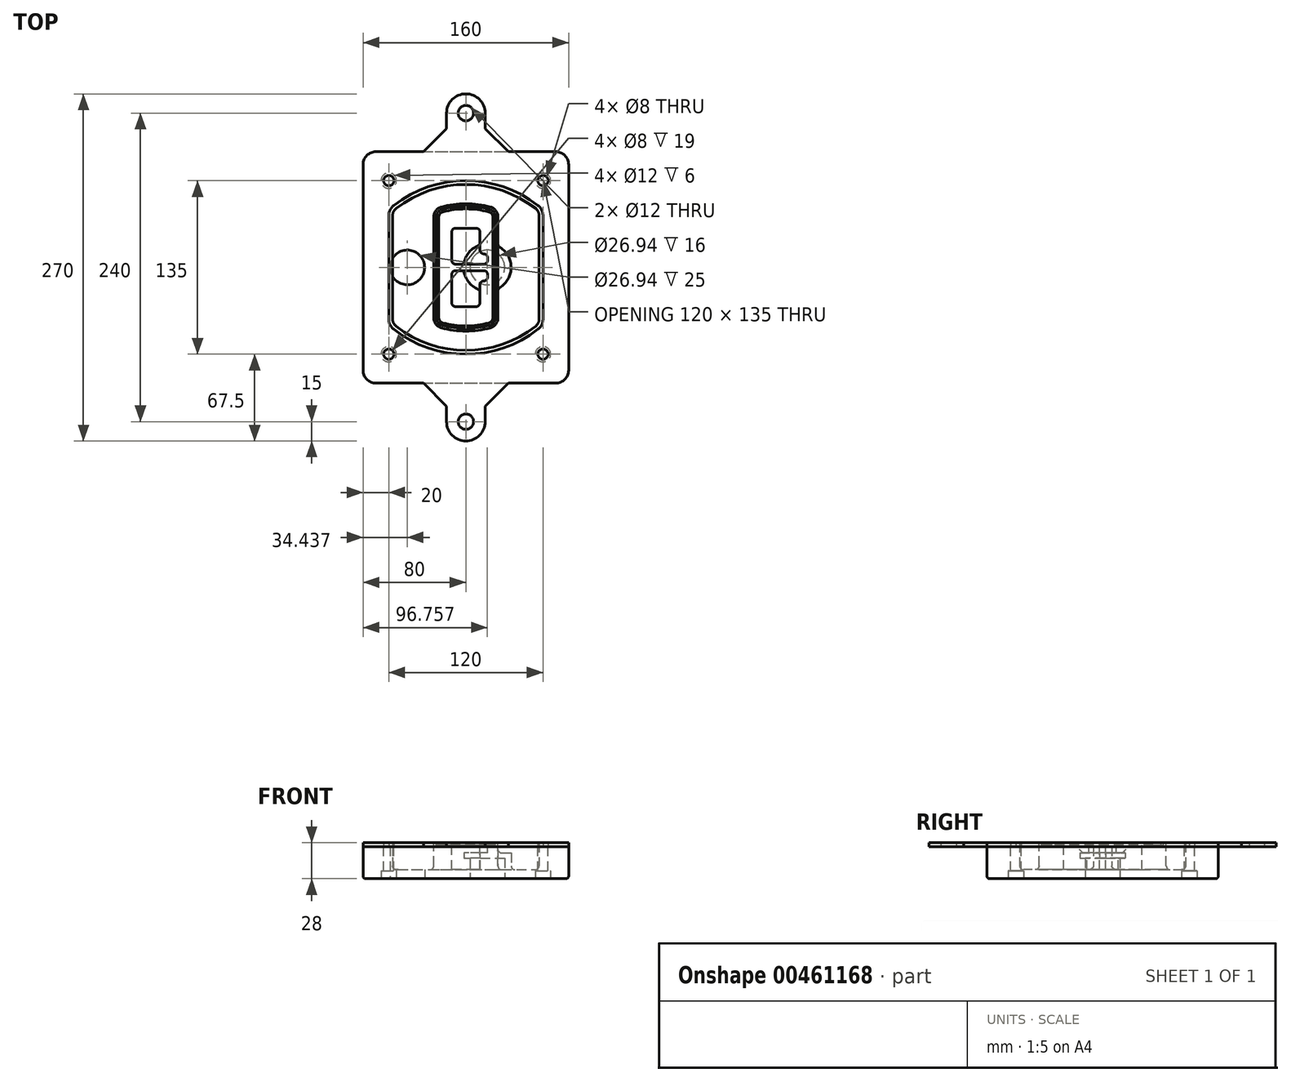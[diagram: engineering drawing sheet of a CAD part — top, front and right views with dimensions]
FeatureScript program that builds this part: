
annotation { "Feature Type Name" : "Feature", "Feature Type Description" : "" }
export const myFeature = defineFeature(function(context is Context, id is Id, definition is map)
    precondition{}
    {
        {
            var Q0;
            Q0=qCreatedBy(makeId("Top.planeOp"),FACE);
            var sketch = newSketch(context, id + "F0", { "sketchPlane" : qUnion([Q0])});
            skPoint(sketch, "E0.rect.middle", {"position": v(0, 0) * mm});
            skLineSegment(sketch, "E1.bottom", {"start": v(-70, -90) * mm, "end": v(70, -90) * mm});
            skLineSegment(sketch, "E1.top", {"start": v(-70, 90) * mm, "end": v(70, 90) * mm});
            skLineSegment(sketch, "E1.left", {"start": v(-80, -80) * mm, "end": v(-80, 80) * mm});
            skLineSegment(sketch, "E1.right", {"start": v(80, -80) * mm, "end": v(80, 80) * mm});
            skLineSegment(sketch, "E2", {"start": v(-80, 90) * mm, "end": v(80, -90) * mm, "construction": true});
            skLineSegment(sketch, "E3", {"start": v(80, 90) * mm, "end": v(-80, -90) * mm, "construction": true});
            skCircle(sketch, "E4", {"center": v(-60, 67.5) * mm, "radius": 4 * mm});
            skCircle(sketch, "E5", {"center": v(60, 67.5) * mm, "radius": 4 * mm});
            skCircle(sketch, "E6", {"center": v(60, -67.5) * mm, "radius": 4 * mm});
            skCircle(sketch, "E7", {"center": v(-60, -67.5) * mm, "radius": 4 * mm});
            skLineSegment(sketch, "E8", {"start": v(-60, 67.5) * mm, "end": v(60, 67.5) * mm, "construction": true});
            skLineSegment(sketch, "E9", {"start": v(60, 67.5) * mm, "end": v(60, -67.5) * mm, "construction": true});
            skLineSegment(sketch, "E10", {"start": v(60, -67.5) * mm, "end": v(-60, -67.5) * mm, "construction": true});
            skLineSegment(sketch, "E11", {"start": v(-60, -67.5) * mm, "end": v(-60, 67.5) * mm, "construction": true});
            skLineSegment(sketch, "E12", {"start": v(-60, 40.3) * mm, "end": v(-60, -40.3) * mm});
            skLineSegment(sketch, "E13", {"start": v(60, 40.3) * mm, "end": v(60, -40.3) * mm});
            skArc(sketch, "E14", {"start": v(56.15, 48.18) * mm, "mid": v(0, 67.5) * mm, "end": v(-56.15, 48.18) * mm});
            skArc(sketch, "E15", {"start": v(-56.15, -48.18) * mm, "mid": v(0, -67.5) * mm, "end": v(56.15, -48.18) * mm});
            skLineSegment(sketch, "E16", {"start": v(-60, 0) * mm, "end": v(60, 0) * mm, "construction": true});
            skPoint(sketch, "E17.visualSharp", {"position": v(-60, -45) * mm});
            skArc(sketch, "E17.filletArc", {"start": v(-60, -40.3) * mm, "mid": v(-58.99, -44.68) * mm, "end": v(-56.15, -48.18) * mm});
            skPoint(sketch, "E18.visualSharp", {"position": v(-60, 45) * mm});
            skArc(sketch, "E18.filletArc", {"start": v(-56.15, 48.18) * mm, "mid": v(-58.99, 44.68) * mm, "end": v(-60, 40.3) * mm});
            skPoint(sketch, "E19.visualSharp", {"position": v(60, 45) * mm});
            skArc(sketch, "E19.filletArc", {"start": v(60, 40.3) * mm, "mid": v(58.99, 44.68) * mm, "end": v(56.15, 48.18) * mm});
            skPoint(sketch, "E20.visualSharp", {"position": v(60, -45) * mm});
            skArc(sketch, "E20.filletArc", {"start": v(56.15, -48.18) * mm, "mid": v(58.99, -44.68) * mm, "end": v(60, -40.3) * mm});
            skPoint(sketch, "E21.visualSharp", {"position": v(-80, 90) * mm});
            skArc(sketch, "E21.filletArc", {"start": v(-70, 90) * mm, "mid": v(-77.07, 87.07) * mm, "end": v(-80, 80) * mm});
            skPoint(sketch, "E22.visualSharp", {"position": v(80, 90) * mm});
            skArc(sketch, "E22.filletArc", {"start": v(80, 80) * mm, "mid": v(77.07, 87.07) * mm, "end": v(70, 90) * mm});
            skPoint(sketch, "E23.visualSharp", {"position": v(80, -90) * mm});
            skArc(sketch, "E23.filletArc", {"start": v(70, -90) * mm, "mid": v(77.07, -87.07) * mm, "end": v(80, -80) * mm});
            skPoint(sketch, "E24.visualSharp", {"position": v(-80, -90) * mm});
            skArc(sketch, "E24.filletArc", {"start": v(-80, -80) * mm, "mid": v(-77.07, -87.07) * mm, "end": v(-70, -90) * mm});
            skArc(sketch, "E25.0", {"start": v(57, 40.3) * mm, "mid": v(56.3, 43.36) * mm, "end": v(54.3, 45.81) * mm});
            skLineSegment(sketch, "E25.1", {"start": v(57, 40.3) * mm, "end": v(57, -40.3) * mm});
            skArc(sketch, "E25.2", {"start": v(54.3, -45.81) * mm, "mid": v(56.3, -43.36) * mm, "end": v(57, -40.3) * mm});
            skArc(sketch, "E25.3", {"start": v(-54.3, -45.81) * mm, "mid": v(0, -64.5) * mm, "end": v(54.3, -45.81) * mm});
            skArc(sketch, "E25.4", {"start": v(-57, -40.3) * mm, "mid": v(-56.3, -43.36) * mm, "end": v(-54.3, -45.81) * mm});
            skArc(sketch, "E25.5", {"start": v(54.3, 45.81) * mm, "mid": v(0, 64.5) * mm, "end": v(-54.3, 45.81) * mm});
            skLineSegment(sketch, "E25.6", {"start": v(-57, 40.3) * mm, "end": v(-57, -40.3) * mm});
            skArc(sketch, "E25.7", {"start": v(-54.3, 45.81) * mm, "mid": v(-56.3, 43.36) * mm, "end": v(-57, 40.3) * mm});
            skArc(sketch, "E26.0", {"start": v(-58.62, 51.33) * mm, "mid": v(-62.58, 46.43) * mm, "end": v(-64, 40.3) * mm});
            skArc(sketch, "E26.1", {"start": v(58.62, 51.33) * mm, "mid": v(0, 71.5) * mm, "end": v(-58.62, 51.33) * mm});
            skArc(sketch, "E26.2", {"start": v(64, 40.3) * mm, "mid": v(62.58, 46.43) * mm, "end": v(58.62, 51.33) * mm});
            skLineSegment(sketch, "E26.3", {"start": v(64, 40.3) * mm, "end": v(64, -40.3) * mm});
            skArc(sketch, "E26.4", {"start": v(58.62, -51.33) * mm, "mid": v(62.58, -46.43) * mm, "end": v(64, -40.3) * mm});
            skLineSegment(sketch, "E26.5", {"start": v(-64, 40.3) * mm, "end": v(-64, -40.3) * mm});
            skArc(sketch, "E26.6", {"start": v(-58.62, -51.33) * mm, "mid": v(0, -71.5) * mm, "end": v(58.62, -51.33) * mm});
            skArc(sketch, "E26.7", {"start": v(-64, -40.3) * mm, "mid": v(-62.58, -46.43) * mm, "end": v(-58.62, -51.33) * mm});
            skSolve(sketch);
        }
        {
            var Q0;
            Q0=makeQuery(id+"F0.imprint","IMPRINT",FACE,{"disambiguationData":[TD([[makeQuery(id+"F0.imprint","IMPRINT",EDGE,{"derivedFrom":sQuery(id+"F0.wireOp",EDGE,"E1.bottom")}),1.0]])]});
            var Q1;
            Q1=makeQuery(id+"F0.imprint","IMPRINT",FACE,{"disambiguationData":[TD([[makeQuery(id+"F0.imprint","IMPRINT",EDGE,{"derivedFrom":sQuery(id+"F0.wireOp",EDGE,"E12")}),1.0]])]});
            var Q2;
            Q2=makeQuery(id+"F0.imprint","IMPRINT",FACE,{"disambiguationData":[TD([[makeQuery(id+"F0.imprint","IMPRINT",EDGE,{"derivedFrom":sQuery(id+"F0.wireOp",EDGE,"E25.0")}),1.0]])]});
            var Q3;
            Q3=makeQuery(id+"F0.imprint","IMPRINT",FACE,{"disambiguationData":[TD([[makeQuery(id+"F0.imprint","IMPRINT",EDGE,{"derivedFrom":sQuery(id+"F0.wireOp",EDGE,"E12")}),-1.0]])]});
            extrude(context, id + "F1", {"entities" : qUnion([Q0, Q1, Q2, Q3]), "oppositeDirection" : true, "depth" : 25 * mm});
        }
        {
            var Q0;
            Q0=makeQuery(id+"F0.imprint","IMPRINT",FACE,{"disambiguationData":[TD([[makeQuery(id+"F0.imprint","IMPRINT",EDGE,{"derivedFrom":sQuery(id+"F0.wireOp",EDGE,"E12")}),1.0]])]});
            extrude(context, id + "F2", {"entities" : qUnion([Q0]), "operationType" : NewBodyOperationType.ADD, "depth" : 3 * mm});
        }
        {
            var Q0;
            Q0=makeQuery(id+"F0.imprint","IMPRINT",FACE,{"disambiguationData":[TD([[makeQuery(id+"F0.imprint","IMPRINT",EDGE,{"derivedFrom":sQuery(id+"F0.wireOp",EDGE,"E25.0")}),1.0]])]});
            extrude(context, id + "F3", {"entities" : qUnion([Q0]), "operationType" : NewBodyOperationType.REMOVE, "oppositeDirection" : true, "depth" : 18 * mm});
        }
        {
            var Q0;
            Q0=makeQuery(id+"F2.opExtrude","CAP_FACE",FACE,{"disambiguationData":[OSD([sQuery(id+"F0.wireOp",EDGE,"E12"),sQuery(id+"F0.wireOp",EDGE,"E13"),sQuery(id+"F0.wireOp",EDGE,"E14"),sQuery(id+"F0.wireOp",EDGE,"E15"),sQuery(id+"F0.wireOp",EDGE,"E17.filletArc"),sQuery(id+"F0.wireOp",EDGE,"E18.filletArc"),sQuery(id+"F0.wireOp",EDGE,"E19.filletArc"),sQuery(id+"F0.wireOp",EDGE,"E20.filletArc"),sQuery(id+"F0.wireOp",EDGE,"E25.0"),sQuery(id+"F0.wireOp",EDGE,"E25.1"),sQuery(id+"F0.wireOp",EDGE,"E25.2"),sQuery(id+"F0.wireOp",EDGE,"E25.3"),sQuery(id+"F0.wireOp",EDGE,"E25.4"),sQuery(id+"F0.wireOp",EDGE,"E25.5"),sQuery(id+"F0.wireOp",EDGE,"E25.6"),sQuery(id+"F0.wireOp",EDGE,"E25.7")])],"isStart":false});
            var sketch = newSketch(context, id + "F4", { "sketchPlane" : qUnion([Q0])});
            skArc(sketch, "E27.0", {"start": v(-19.08, -46.97) * mm, "mid": v(0, -49.5) * mm, "end": v(19.08, -46.97) * mm});
            skArc(sketch, "E28.0", {"start": v(19.08, 46.97) * mm, "mid": v(0, 49.5) * mm, "end": v(-19.08, 46.97) * mm});
            skLineSegment(sketch, "E29", {"start": v(-25, 39.25) * mm, "end": v(-25, -39.25) * mm});
            skLineSegment(sketch, "E30", {"start": v(25, 39.25) * mm, "end": v(25, -39.25) * mm});
            skLineSegment(sketch, "E31", {"start": v(-25, 45.1) * mm, "end": v(25, 45.1) * mm, "construction": true});
            skLineSegment(sketch, "E32", {"start": v(-25, -45.1) * mm, "end": v(25, -45.1) * mm, "construction": true});
            skPoint(sketch, "E33.visualSharp", {"position": v(-25, 45.1) * mm});
            skArc(sketch, "E33.filletArc", {"start": v(-19.08, 46.97) * mm, "mid": v(-23.35, 44.11) * mm, "end": v(-25, 39.25) * mm});
            skPoint(sketch, "E34.visualSharp", {"position": v(25, 45.1) * mm});
            skArc(sketch, "E34.filletArc", {"start": v(25, 39.25) * mm, "mid": v(23.35, 44.11) * mm, "end": v(19.08, 46.97) * mm});
            skPoint(sketch, "E35.visualSharp", {"position": v(25, -45.1) * mm});
            skArc(sketch, "E35.filletArc", {"start": v(19.08, -46.97) * mm, "mid": v(23.35, -44.11) * mm, "end": v(25, -39.25) * mm});
            skPoint(sketch, "E36.visualSharp", {"position": v(-25, -45.1) * mm});
            skArc(sketch, "E36.filletArc", {"start": v(-25, -39.25) * mm, "mid": v(-23.35, -44.11) * mm, "end": v(-19.08, -46.97) * mm});
            skArc(sketch, "E37.0", {"start": v(54.3, 45.81) * mm, "mid": v(0, 64.5) * mm, "end": v(-54.3, 45.81) * mm});
            skArc(sketch, "E37.1", {"start": v(-54.3, 45.81) * mm, "mid": v(-56.3, 43.36) * mm, "end": v(-57, 40.3) * mm});
            skLineSegment(sketch, "E37.2", {"start": v(-57, 40.3) * mm, "end": v(-57, -40.3) * mm});
            skArc(sketch, "E37.3", {"start": v(-57, -40.3) * mm, "mid": v(-56.3, -43.36) * mm, "end": v(-54.3, -45.81) * mm});
            skArc(sketch, "E37.4", {"start": v(-54.3, -45.81) * mm, "mid": v(0, -64.5) * mm, "end": v(54.3, -45.81) * mm});
            skArc(sketch, "E37.5", {"start": v(54.3, -45.81) * mm, "mid": v(56.3, -43.36) * mm, "end": v(57, -40.3) * mm});
            skLineSegment(sketch, "E37.6", {"start": v(57, 40.3) * mm, "end": v(57, -40.3) * mm});
            skArc(sketch, "E37.7", {"start": v(57, 40.3) * mm, "mid": v(56.3, 43.36) * mm, "end": v(54.3, 45.81) * mm});
            skLineSegment(sketch, "E38.0", {"start": v(23, 39.25) * mm, "end": v(23, -39.25) * mm});
            skArc(sketch, "E38.1", {"start": v(18.56, -45.04) * mm, "mid": v(21.76, -42.9) * mm, "end": v(23, -39.25) * mm});
            skArc(sketch, "E38.2", {"start": v(-18.56, -45.04) * mm, "mid": v(0, -47.5) * mm, "end": v(18.56, -45.04) * mm});
            skArc(sketch, "E38.3", {"start": v(-23, -39.25) * mm, "mid": v(-21.76, -42.9) * mm, "end": v(-18.56, -45.04) * mm});
            skLineSegment(sketch, "E38.4", {"start": v(-23, 39.25) * mm, "end": v(-23, -39.25) * mm});
            skArc(sketch, "E38.5", {"start": v(23, 39.25) * mm, "mid": v(21.76, 42.9) * mm, "end": v(18.56, 45.04) * mm});
            skArc(sketch, "E38.6", {"start": v(-18.56, 45.04) * mm, "mid": v(-21.76, 42.9) * mm, "end": v(-23, 39.25) * mm});
            skArc(sketch, "E38.7", {"start": v(18.56, 45.04) * mm, "mid": v(0, 47.5) * mm, "end": v(-18.56, 45.04) * mm});
            skArc(sketch, "E39.0", {"start": v(21, 39.25) * mm, "mid": v(20.18, 41.68) * mm, "end": v(18.04, 43.1) * mm});
            skLineSegment(sketch, "E39.1", {"start": v(21, 39.25) * mm, "end": v(21, -39.25) * mm});
            skArc(sketch, "E39.2", {"start": v(18.04, -43.1) * mm, "mid": v(20.18, -41.68) * mm, "end": v(21, -39.25) * mm});
            skArc(sketch, "E39.3", {"start": v(-18.04, -43.1) * mm, "mid": v(0, -45.5) * mm, "end": v(18.04, -43.1) * mm});
            skArc(sketch, "E39.4", {"start": v(-21, -39.25) * mm, "mid": v(-20.18, -41.68) * mm, "end": v(-18.04, -43.1) * mm});
            skArc(sketch, "E39.5", {"start": v(18.04, 43.1) * mm, "mid": v(0, 45.5) * mm, "end": v(-18.04, 43.1) * mm});
            skLineSegment(sketch, "E39.6", {"start": v(-21, 39.25) * mm, "end": v(-21, -39.25) * mm});
            skArc(sketch, "E39.7", {"start": v(-18.04, 43.1) * mm, "mid": v(-20.18, 41.68) * mm, "end": v(-21, 39.25) * mm});
            skLineSegment(sketch, "E40", {"start": v(-25, 0) * mm, "end": v(25, 0) * mm, "construction": true});
            skLineSegment(sketch, "E41", {"start": v(-11, 5.5) * mm, "end": v(-11, 27.5) * mm});
            skLineSegment(sketch, "E42", {"start": v(-8, 30.5) * mm, "end": v(8, 30.5) * mm});
            skLineSegment(sketch, "E43", {"start": v(11, 27.5) * mm, "end": v(11, 13.5) * mm});
            skLineSegment(sketch, "E44", {"start": v(14, 10.5) * mm, "end": v(14, 10.5) * mm});
            skLineSegment(sketch, "E45", {"start": v(17, 7.5) * mm, "end": v(17, 5.5) * mm});
            skLineSegment(sketch, "E46", {"start": v(14, 2.5) * mm, "end": v(-8, 2.5) * mm});
            skPoint(sketch, "E47.visualSharp", {"position": v(-11, 30.5) * mm});
            skArc(sketch, "E47.filletArc", {"start": v(-8, 30.5) * mm, "mid": v(-10.12, 29.62) * mm, "end": v(-11, 27.5) * mm});
            skPoint(sketch, "E48.visualSharp", {"position": v(11, 30.5) * mm});
            skArc(sketch, "E48.filletArc", {"start": v(11, 27.5) * mm, "mid": v(10.12, 29.62) * mm, "end": v(8, 30.5) * mm});
            skPoint(sketch, "E49.visualSharp", {"position": v(11, 10.5) * mm});
            skArc(sketch, "E49.filletArc", {"start": v(11, 13.5) * mm, "mid": v(11.88, 11.38) * mm, "end": v(14, 10.5) * mm});
            skPoint(sketch, "E50.visualSharp", {"position": v(17, 10.5) * mm});
            skArc(sketch, "E50.filletArc", {"start": v(17, 7.5) * mm, "mid": v(16.12, 9.62) * mm, "end": v(14, 10.5) * mm});
            skPoint(sketch, "E51.visualSharp", {"position": v(17, 2.5) * mm});
            skArc(sketch, "E51.filletArc", {"start": v(14, 2.5) * mm, "mid": v(16.12, 3.38) * mm, "end": v(17, 5.5) * mm});
            skPoint(sketch, "E52.visualSharp", {"position": v(-11, 2.5) * mm});
            skArc(sketch, "E52.filletArc", {"start": v(-11, 5.5) * mm, "mid": v(-10.12, 3.38) * mm, "end": v(-8, 2.5) * mm});
            skLineSegment(sketch, "E53.0.MirrorCS", {"start": v(14, -2.5) * mm, "end": v(-8, -2.5) * mm});
            skArc(sketch, "E54.0.MirrorCS", {"start": v(-11, -5.5) * mm, "mid": v(-10.12, -3.38) * mm, "end": v(-8, -2.5) * mm});
            skLineSegment(sketch, "E55.0.MirrorCS", {"start": v(-11, -5.5) * mm, "end": v(-11, -27.5) * mm});
            skArc(sketch, "E56.0.MirrorCS", {"start": v(-8, -30.5) * mm, "mid": v(-10.12, -29.62) * mm, "end": v(-11, -27.5) * mm});
            skLineSegment(sketch, "E57.0.MirrorCS", {"start": v(-8, -30.5) * mm, "end": v(8, -30.5) * mm});
            skArc(sketch, "E58.0.MirrorCS", {"start": v(11, -27.5) * mm, "mid": v(10.12, -29.62) * mm, "end": v(8, -30.5) * mm});
            skLineSegment(sketch, "E59.0.MirrorCS", {"start": v(11, -27.5) * mm, "end": v(11, -13.5) * mm});
            skArc(sketch, "E60.0.MirrorCS", {"start": v(11, -13.5) * mm, "mid": v(11.88, -11.38) * mm, "end": v(14, -10.5) * mm});
            skArc(sketch, "E61.0.MirrorCS", {"start": v(17, -7.5) * mm, "mid": v(16.12, -9.62) * mm, "end": v(14, -10.5) * mm});
            skLineSegment(sketch, "E62.0.MirrorCS", {"start": v(17, -7.5) * mm, "end": v(17, -5.5) * mm});
            skArc(sketch, "E63.0.MirrorCS", {"start": v(14, -2.5) * mm, "mid": v(16.12, -3.38) * mm, "end": v(17, -5.5) * mm});
            skSolve(sketch);
        }
        {
            var Q0;
            Q0=makeQuery(id+"F4.imprint","IMPRINT",FACE,{"disambiguationData":[TD([[makeQuery(id+"F4.imprint","IMPRINT",EDGE,{"derivedFrom":sQuery(id+"F4.wireOp",EDGE,"E27.0")}),1.0]])]});
            var Q1;
            Q1=makeQuery(id+"F4.imprint","IMPRINT",FACE,{"disambiguationData":[TD([[makeQuery(id+"F4.imprint","IMPRINT",EDGE,{"derivedFrom":sQuery(id+"F4.wireOp",EDGE,"E38.0")}),-1.0]])]});
            var Q2;
            Q2=makeQuery(id+"F4.imprint","IMPRINT",FACE,{"disambiguationData":[TD([[makeQuery(id+"F4.imprint","IMPRINT",EDGE,{"derivedFrom":sQuery(id+"F4.wireOp",EDGE,"E39.0")}),1.0]])]});
            extrude(context, id + "F5", {"entities" : qUnion([Q0, Q1, Q2]), "operationType" : NewBodyOperationType.ADD, "endBound" : BoundingType.UP_TO_NEXT, "oppositeDirection" : true, "depth" : 25 * mm});
        }
        {
            var Q0;
            Q0=makeQuery(id+"F4.imprint","IMPRINT",FACE,{"disambiguationData":[TD([[makeQuery(id+"F4.imprint","IMPRINT",EDGE,{"derivedFrom":sQuery(id+"F4.wireOp",EDGE,"E38.0")}),-1.0]])]});
            extrude(context, id + "F6", {"entities" : qUnion([Q0]), "operationType" : NewBodyOperationType.REMOVE, "oppositeDirection" : true, "depth" : 2 * mm});
        }
        {
            var Q0;
            Q0=makeQuery(id+"F1.opExtrude","CAP_FACE",FACE,{"disambiguationData":[OSD([sQuery(id+"F0.wireOp",EDGE,"E1.bottom"),sQuery(id+"F0.wireOp",EDGE,"E1.top"),sQuery(id+"F0.wireOp",EDGE,"E1.left"),sQuery(id+"F0.wireOp",EDGE,"E1.right"),sQuery(id+"F0.wireOp",EDGE,"E4"),sQuery(id+"F0.wireOp",EDGE,"E5"),sQuery(id+"F0.wireOp",EDGE,"E6"),sQuery(id+"F0.wireOp",EDGE,"E7"),sQuery(id+"F0.wireOp",EDGE,"E21.filletArc"),sQuery(id+"F0.wireOp",EDGE,"E22.filletArc"),sQuery(id+"F0.wireOp",EDGE,"E23.filletArc"),sQuery(id+"F0.wireOp",EDGE,"E24.filletArc")])],"isStart":false});
            var sketch = newSketch(context, id + "F7", { "sketchPlane" : qUnion([Q0])});
            skCircle(sketch, "E64", {"center": v(16.76, 0) * mm, "radius": 13.47 * mm});
            skCircle(sketch, "E65", {"center": v(-45.56, 0) * mm, "radius": 13.47 * mm});
            skLineSegment(sketch, "E66", {"start": v(80, 0) * mm, "end": v(-80, 0) * mm});
            skCircle(sketch, "E67", {"center": v(16.76, 0) * mm, "radius": 18.47 * mm});
            skCircle(sketch, "E68", {"center": v(60, -67.5) * mm, "radius": 6 * mm});
            skCircle(sketch, "E69", {"center": v(-60, -67.5) * mm, "radius": 6 * mm});
            skCircle(sketch, "E70", {"center": v(-60, 67.5) * mm, "radius": 6 * mm});
            skCircle(sketch, "E71", {"center": v(60, 67.5) * mm, "radius": 6 * mm});
            skSolve(sketch);
        }
        {
            var Q0;
            {var subQ1=sQuery(id+"F7.wireOp",EDGE,"E66");var subQ4=sQuery(id+"F7.wireOp",EDGE,"E64");var subQ6=makeQuery(id+"F7.imprint","INTERSECT",VERTEX,{"disambiguationData":[OD(0.0)],"derivedFrom":[subQ4,subQ1]});Q0=makeQuery(id+"F7.imprint","IMPRINT",FACE,{"disambiguationData":[TD([[makeQuery(id+"F7.imprint","IMPRINT",EDGE,{"disambiguationData":[TD([[subQ6,-1.0]])],"derivedFrom":subQ4}),-1.0]])]});}
            var Q1;
            {var subQ0=sQuery(id+"F7.wireOp",EDGE,"E66");var subQ1=sQuery(id+"F7.wireOp",EDGE,"E64");var subQ3=makeQuery(id+"F7.imprint","INTERSECT",VERTEX,{"disambiguationData":[OD(0.0)],"derivedFrom":[subQ1,subQ0]});Q1=makeQuery(id+"F7.imprint","IMPRINT",FACE,{"disambiguationData":[TD([[makeQuery(id+"F7.imprint","IMPRINT",EDGE,{"disambiguationData":[TD([[subQ3,-1.0]])],"derivedFrom":subQ1}),1.0]])]});}
            var Q2;
            {var subQ0=sQuery(id+"F7.wireOp",EDGE,"E66");var subQ1=sQuery(id+"F7.wireOp",EDGE,"E64");var subQ3=makeQuery(id+"F7.imprint","INTERSECT",VERTEX,{"disambiguationData":[OD(0.0)],"derivedFrom":[subQ1,subQ0]});Q2=makeQuery(id+"F7.imprint","IMPRINT",FACE,{"disambiguationData":[TD([[makeQuery(id+"F7.imprint","IMPRINT",EDGE,{"disambiguationData":[TD([[subQ3,1.0]])],"derivedFrom":subQ1}),1.0]])]});}
            var Q3;
            {var subQ1=sQuery(id+"F7.wireOp",EDGE,"E66");var subQ4=sQuery(id+"F7.wireOp",EDGE,"E64");var subQ6=makeQuery(id+"F7.imprint","INTERSECT",VERTEX,{"disambiguationData":[OD(0.0)],"derivedFrom":[subQ4,subQ1]});Q3=makeQuery(id+"F7.imprint","IMPRINT",FACE,{"disambiguationData":[TD([[makeQuery(id+"F7.imprint","IMPRINT",EDGE,{"disambiguationData":[TD([[subQ6,1.0]])],"derivedFrom":subQ4}),-1.0]])]});}
            extrude(context, id + "F8", {"entities" : qUnion([Q0, Q1, Q2, Q3]), "operationType" : NewBodyOperationType.ADD, "oppositeDirection" : true, "depth" : 20 * mm});
        }
        {
            var Q0;
            {var subQ0=sQuery(id+"F7.wireOp",EDGE,"E66");var subQ1=sQuery(id+"F7.wireOp",EDGE,"E64");var subQ3=makeQuery(id+"F7.imprint","INTERSECT",VERTEX,{"disambiguationData":[OD(0.0)],"derivedFrom":[subQ1,subQ0]});Q0=makeQuery(id+"F7.imprint","IMPRINT",FACE,{"disambiguationData":[TD([[makeQuery(id+"F7.imprint","IMPRINT",EDGE,{"disambiguationData":[TD([[subQ3,-1.0]])],"derivedFrom":subQ1}),1.0]])]});}
            var Q1;
            {var subQ0=sQuery(id+"F7.wireOp",EDGE,"E66");var subQ1=sQuery(id+"F7.wireOp",EDGE,"E64");var subQ3=makeQuery(id+"F7.imprint","INTERSECT",VERTEX,{"disambiguationData":[OD(0.0)],"derivedFrom":[subQ1,subQ0]});Q1=makeQuery(id+"F7.imprint","IMPRINT",FACE,{"disambiguationData":[TD([[makeQuery(id+"F7.imprint","IMPRINT",EDGE,{"disambiguationData":[TD([[subQ3,1.0]])],"derivedFrom":subQ1}),1.0]])]});}
            extrude(context, id + "F9", {"entities" : qUnion([Q0, Q1]), "operationType" : NewBodyOperationType.REMOVE, "oppositeDirection" : true, "depth" : 16 * mm});
        }
        {
            var Q0;
            {var subQ0=sQuery(id+"F7.wireOp",EDGE,"E66");var subQ1=sQuery(id+"F7.wireOp",EDGE,"E65");var subQ3=makeQuery(id+"F7.imprint","INTERSECT",VERTEX,{"disambiguationData":[OD(0.0)],"derivedFrom":[subQ1,subQ0]});Q0=makeQuery(id+"F7.imprint","IMPRINT",FACE,{"disambiguationData":[TD([[makeQuery(id+"F7.imprint","IMPRINT",EDGE,{"disambiguationData":[TD([[subQ3,-1.0]])],"derivedFrom":subQ1}),1.0]])]});}
            var Q1;
            {var subQ0=sQuery(id+"F7.wireOp",EDGE,"E66");var subQ1=sQuery(id+"F7.wireOp",EDGE,"E65");var subQ3=makeQuery(id+"F7.imprint","INTERSECT",VERTEX,{"disambiguationData":[OD(0.0)],"derivedFrom":[subQ1,subQ0]});Q1=makeQuery(id+"F7.imprint","IMPRINT",FACE,{"disambiguationData":[TD([[makeQuery(id+"F7.imprint","IMPRINT",EDGE,{"disambiguationData":[TD([[subQ3,1.0]])],"derivedFrom":subQ1}),1.0]])]});}
            extrude(context, id + "F10", {"entities" : qUnion([Q0, Q1]), "operationType" : NewBodyOperationType.REMOVE, "oppositeDirection" : true, "depth" : 25 * mm});
        }
        {
            var Q0;
            Q0=makeQuery(id+"F7.imprint","IMPRINT",FACE,{"disambiguationData":[TD([[makeQuery(id+"F7.imprint","IMPRINT",EDGE,{"derivedFrom":sQuery(id+"F7.wireOp",EDGE,"E68")}),1.0]])]});
            var Q1;
            Q1=makeQuery(id+"F7.imprint","IMPRINT",FACE,{"disambiguationData":[TD([[makeQuery(id+"F7.imprint","IMPRINT",EDGE,{"derivedFrom":makeQuery(id+"F1.opExtrude","CAP_EDGE",EDGE,{"disambiguationData":[OSD([sQuery(id+"F0.wireOp",EDGE,"E5")])],"isStart":false})}),-1.0]])]});
            var Q2;
            Q2=makeQuery(id+"F7.imprint","IMPRINT",FACE,{"disambiguationData":[TD([[makeQuery(id+"F7.imprint","IMPRINT",EDGE,{"derivedFrom":sQuery(id+"F7.wireOp",EDGE,"E69")}),1.0]])]});
            var Q3;
            Q3=makeQuery(id+"F7.imprint","IMPRINT",FACE,{"disambiguationData":[TD([[makeQuery(id+"F7.imprint","IMPRINT",EDGE,{"derivedFrom":makeQuery(id+"F1.opExtrude","CAP_EDGE",EDGE,{"disambiguationData":[OSD([sQuery(id+"F0.wireOp",EDGE,"E4")])],"isStart":false})}),-1.0]])]});
            var Q4;
            Q4=makeQuery(id+"F7.imprint","IMPRINT",FACE,{"disambiguationData":[TD([[makeQuery(id+"F7.imprint","IMPRINT",EDGE,{"derivedFrom":sQuery(id+"F7.wireOp",EDGE,"E70")}),1.0]])]});
            var Q5;
            Q5=makeQuery(id+"F7.imprint","IMPRINT",FACE,{"disambiguationData":[TD([[makeQuery(id+"F7.imprint","IMPRINT",EDGE,{"derivedFrom":makeQuery(id+"F1.opExtrude","CAP_EDGE",EDGE,{"disambiguationData":[OSD([sQuery(id+"F0.wireOp",EDGE,"E7")])],"isStart":false})}),-1.0]])]});
            var Q6;
            Q6=makeQuery(id+"F7.imprint","IMPRINT",FACE,{"disambiguationData":[TD([[makeQuery(id+"F7.imprint","IMPRINT",EDGE,{"derivedFrom":sQuery(id+"F7.wireOp",EDGE,"E71")}),1.0]])]});
            var Q7;
            Q7=makeQuery(id+"F7.imprint","IMPRINT",FACE,{"disambiguationData":[TD([[makeQuery(id+"F7.imprint","IMPRINT",EDGE,{"derivedFrom":makeQuery(id+"F1.opExtrude","CAP_EDGE",EDGE,{"disambiguationData":[OSD([sQuery(id+"F0.wireOp",EDGE,"E6")])],"isStart":false})}),-1.0]])]});
            extrude(context, id + "F11", {"entities" : qUnion([Q0, Q1, Q2, Q3, Q4, Q5, Q6, Q7]), "operationType" : NewBodyOperationType.REMOVE, "oppositeDirection" : true, "depth" : 6 * mm});
        }
        {
            var Q0;
            Q0=makeQuery(id+"F9.boolean.opBoolean","COPY",FACE,{"derivedFrom":makeQuery(id+"F9.opExtrude","CAP_FACE",FACE,{"disambiguationData":[OSD([sQuery(id+"F7.wireOp",EDGE,"E64")])],"isStart":false})});
            var sketch = newSketch(context, id + "F12", { "sketchPlane" : qUnion([Q0])});
            skArc(sketch, "E72.0", {"start": v(11, 17.55) * mm, "mid": v(2.57, 11.82) * mm, "end": v(-1.54, 2.5) * mm});
            skArc(sketch, "E72.1", {"start": v(-1.54, -2.5) * mm, "mid": v(2.57, -11.82) * mm, "end": v(11, -17.55) * mm});
            skLineSegment(sketch, "E73", {"start": v(-1.54, -2.5) * mm, "end": v(14, -2.5) * mm});
            skLineSegment(sketch, "E74.0", {"start": v(14, 2.5) * mm, "end": v(-1.54, 2.5) * mm});
            skArc(sketch, "E74.1", {"start": v(14, 2.5) * mm, "mid": v(16.12, 3.38) * mm, "end": v(17, 5.5) * mm});
            skLineSegment(sketch, "E74.2", {"start": v(17, 7.5) * mm, "end": v(17, 5.5) * mm});
            skArc(sketch, "E74.3", {"start": v(17, 7.5) * mm, "mid": v(16.12, 9.62) * mm, "end": v(14, 10.5) * mm});
            skArc(sketch, "E74.4", {"start": v(11, 13.5) * mm, "mid": v(11.88, 11.38) * mm, "end": v(14, 10.5) * mm});
            skLineSegment(sketch, "E74.5", {"start": v(11, 17.55) * mm, "end": v(11, 13.5) * mm});
            skLineSegment(sketch, "E74.7", {"start": v(14, -2.5) * mm, "end": v(-1.54, -2.5) * mm});
            skArc(sketch, "E74.8", {"start": v(14, -2.5) * mm, "mid": v(16.12, -3.38) * mm, "end": v(17, -5.5) * mm});
            skLineSegment(sketch, "E74.9", {"start": v(17, -7.5) * mm, "end": v(17, -5.5) * mm});
            skArc(sketch, "E74.10", {"start": v(17, -7.5) * mm, "mid": v(16.12, -9.62) * mm, "end": v(14, -10.5) * mm});
            skArc(sketch, "E74.11", {"start": v(11, -13.5) * mm, "mid": v(11.88, -11.38) * mm, "end": v(14, -10.5) * mm});
            skLineSegment(sketch, "E74.12", {"start": v(11, -17.55) * mm, "end": v(11, -13.5) * mm});
            skPoint(sketch, "E75.orphan", {"position": v(11, -27.5) * mm});
            skPoint(sketch, "E76.orphan", {"position": v(-8, -2.5) * mm});
            skPoint(sketch, "E77.orphan", {"position": v(-8, 2.5) * mm});
            skPoint(sketch, "E78.orphan", {"position": v(11, 27.5) * mm});
            skSolve(sketch);
        }
        {
            var Q0;
            {var subQ7=sQuery(id+"F12.wireOp",EDGE,"E72.0");var subQ14=sQuery(id+"F12.wireOp",EDGE,"E72.1");var subQ16=sQuery(id+"F12.wireOp",EDGE,"E74.1");var subQ18=sQuery(id+"F12.wireOp",EDGE,"E74.8");Q0=qUnion([makeQuery(id+"F12.imprint","IMPRINT",FACE,{"disambiguationData":[TD([[makeQuery(id+"F12.imprint","IMPRINT",EDGE,{"derivedFrom":subQ7}),1.0]])]}),makeQuery(id+"F12.imprint","IMPRINT",FACE,{"disambiguationData":[TD([[makeQuery(id+"F12.imprint","IMPRINT",EDGE,{"derivedFrom":subQ14}),1.0]])]}),makeQuery(id+"F12.imprint","IMPRINT",FACE,{"disambiguationData":[TD([[makeQuery(id+"F12.imprint","IMPRINT",EDGE,{"derivedFrom":subQ16}),1.0]])]}),makeQuery(id+"F12.imprint","IMPRINT",FACE,{"disambiguationData":[TD([[makeQuery(id+"F12.imprint","IMPRINT",EDGE,{"derivedFrom":subQ18}),-1.0]])]})]);}
            var Q1;
            Q1=makeQuery(id+"F5.boolean.opBoolean","SPLIT",FACE,{"disambiguationData":[TD([makeQuery(id+"F5.opExtrude","SWEPT_FACE",FACE,{"disambiguationData":[OSD([sQuery(id+"F4.wireOp",EDGE,"E41")])]})])],"derivedFrom":makeQuery(id+"F3.boolean.opBoolean","COPY",FACE,{"derivedFrom":makeQuery(id+"F3.opExtrude","CAP_FACE",FACE,{"disambiguationData":[OSD([sQuery(id+"F0.wireOp",EDGE,"E25.0"),sQuery(id+"F0.wireOp",EDGE,"E25.1"),sQuery(id+"F0.wireOp",EDGE,"E25.2"),sQuery(id+"F0.wireOp",EDGE,"E25.3"),sQuery(id+"F0.wireOp",EDGE,"E25.4"),sQuery(id+"F0.wireOp",EDGE,"E25.5"),sQuery(id+"F0.wireOp",EDGE,"E25.6"),sQuery(id+"F0.wireOp",EDGE,"E25.7")])],"isStart":false})})});
            extrude(context, id + "F13", {"entities" : qUnion([Q0]), "operationType" : NewBodyOperationType.REMOVE, "endBound" : BoundingType.UP_TO_SURFACE, "endBoundEntityFace" : qUnion([Q1]), "depth" : 25 * mm});
        }
        {
            var Q0;
            Q0=makeQuery(id+"F3.boolean.opBoolean","COPY",EDGE,{"derivedFrom":makeQuery(id+"F3.opExtrude","CAP_EDGE",EDGE,{"disambiguationData":[OSD([sQuery(id+"F0.wireOp",EDGE,"E25.6")])],"isStart":false})});
            var Q1;
            Q1=makeQuery(id+"F8.boolean.opBoolean","INTERSECT",EDGE,{"derivedFrom":[makeQuery(id+"F5.opExtrude","SWEPT_FACE",FACE,{"disambiguationData":[OSD([sQuery(id+"F4.wireOp",EDGE,"E30")])]}),makeQuery(id+"F8.opExtrude","CAP_FACE",FACE,{"disambiguationData":[OSD([sQuery(id+"F7.wireOp",EDGE,"E67")])],"isStart":false})]});
            var Q2;
            Q2=makeQuery(id+"F8.boolean.opBoolean","INTERSECT",EDGE,{"disambiguationData":[OD(1.0)],"derivedFrom":[makeQuery(id+"F5.opExtrude","SWEPT_FACE",FACE,{"disambiguationData":[OSD([sQuery(id+"F4.wireOp",EDGE,"E30")])]}),makeQuery(id+"F8.opExtrude","SWEPT_FACE",FACE,{"disambiguationData":[OSD([sQuery(id+"F7.wireOp",EDGE,"E67")])]})]});
            var Q3;
            {var subQ0=sQuery(id+"F4.wireOp",EDGE,"E30");Q3=makeQuery(id+"F8.boolean.opBoolean","SPLIT",EDGE,{"disambiguationData":[TD([makeQuery(id+"F5.opExtrude","SWEPT_FACE",FACE,{"disambiguationData":[OSD([sQuery(id+"F4.wireOp",EDGE,"E35.filletArc")])]})])],"derivedFrom":makeQuery(id+"F5.opExtrude","CAP_EDGE",EDGE,{"disambiguationData":[OSD([subQ0])],"isStart":false})});}
            var Q4;
            {var subQ0=sQuery(id+"F0.wireOp",EDGE,"E25.7");var subQ1=sQuery(id+"F0.wireOp",EDGE,"E25.1");var subQ2=sQuery(id+"F0.wireOp",EDGE,"E25.6");var subQ3=sQuery(id+"F0.wireOp",EDGE,"E25.5");var subQ4=sQuery(id+"F0.wireOp",EDGE,"E25.4");var subQ5=sQuery(id+"F0.wireOp",EDGE,"E25.0");var subQ6=sQuery(id+"F0.wireOp",EDGE,"E25.2");var subQ7=sQuery(id+"F0.wireOp",EDGE,"E25.3");Q4=makeQuery(id+"F8.boolean.opBoolean","INTERSECT",EDGE,{"derivedFrom":[makeQuery(id+"F5.boolean.opBoolean","SPLIT",FACE,{"disambiguationData":[TD([makeQuery(id+"F2.opExtrude","SWEPT_FACE",FACE,{"disambiguationData":[OSD([subQ5])]})])],"derivedFrom":makeQuery(id+"F3.boolean.opBoolean","COPY",FACE,{"derivedFrom":makeQuery(id+"F3.opExtrude","CAP_FACE",FACE,{"disambiguationData":[OSD([subQ5,subQ1,subQ6,subQ7,subQ4,subQ3,subQ2,subQ0])],"isStart":false})})}),makeQuery(id+"F8.opExtrude","SWEPT_FACE",FACE,{"disambiguationData":[OSD([sQuery(id+"F7.wireOp",EDGE,"E67")])]})]});}
            var Q5;
            Q5=makeQuery(id+"F8.boolean.opBoolean","INTERSECT",EDGE,{"disambiguationData":[OD(0.0)],"derivedFrom":[makeQuery(id+"F5.opExtrude","SWEPT_FACE",FACE,{"disambiguationData":[OSD([sQuery(id+"F4.wireOp",EDGE,"E30")])]}),makeQuery(id+"F8.opExtrude","SWEPT_FACE",FACE,{"disambiguationData":[OSD([sQuery(id+"F7.wireOp",EDGE,"E67")])]})]});
            fillet(context, id + "F14", {"entities" : qUnion([Q0, Q1, Q2, Q3, Q4, Q5]), "radius" : 3 * mm, "tangentPropagation" : true, "allowEdgeOverflow" : false});
        }
        {
            var Q0;
            Q0=makeQuery(id+"F1.opExtrude","CAP_EDGE",EDGE,{"disambiguationData":[OSD([sQuery(id+"F0.wireOp",EDGE,"E1.bottom")])],"isStart":false});
            fillet(context, id + "F15", {"entities" : qUnion([Q0]), "radius" : 2 * mm, "tangentPropagation" : true, "allowEdgeOverflow" : false});
        }
        {
            var Q0;
            {var subQ0=sQuery(id+"F0.wireOp",EDGE,"E21.filletArc");var subQ1=sQuery(id+"F0.wireOp",EDGE,"E7");var subQ2=sQuery(id+"F0.wireOp",EDGE,"E6");var subQ3=sQuery(id+"F0.wireOp",EDGE,"E5");var subQ4=sQuery(id+"F0.wireOp",EDGE,"E4");var subQ5=sQuery(id+"F0.wireOp",EDGE,"E22.filletArc");var subQ6=sQuery(id+"F0.wireOp",EDGE,"E1.bottom");var subQ7=sQuery(id+"F0.wireOp",EDGE,"E1.right");var subQ8=sQuery(id+"F0.wireOp",EDGE,"E1.top");var subQ9=sQuery(id+"F0.wireOp",EDGE,"E1.left");var subQ10=sQuery(id+"F0.wireOp",EDGE,"E23.filletArc");var subQ11=sQuery(id+"F0.wireOp",EDGE,"E24.filletArc");Q0=makeQuery(id+"F2.boolean.opBoolean","SPLIT",FACE,{"disambiguationData":[TD([makeQuery(id+"F1.opExtrude","SWEPT_FACE",FACE,{"disambiguationData":[OSD([subQ6])]})])],"derivedFrom":makeQuery(id+"F1.opExtrude","CAP_FACE",FACE,{"disambiguationData":[OSD([subQ6,subQ8,subQ9,subQ7,subQ4,subQ3,subQ2,subQ1,subQ0,subQ5,subQ10,subQ11])],"isStart":true})});}
            var sketch = newSketch(context, id + "F16", { "sketchPlane" : qUnion([Q0])});
            skArc(sketch, "E79.1", {"start": v(-70, 90) * mm, "mid": v(-77.07, 87.07) * mm, "end": v(-80, 80) * mm});
            skLineSegment(sketch, "E79.2", {"start": v(-80, -80) * mm, "end": v(-80, 80) * mm});
            skArc(sketch, "E79.3", {"start": v(-80, -80) * mm, "mid": v(-77.07, -87.07) * mm, "end": v(-70, -90) * mm});
            skLineSegment(sketch, "E79.4", {"start": v(-70, -90) * mm, "end": v(70, -90) * mm});
            skCircle(sketch, "E79.5", {"center": v(-60, -67.5) * mm, "radius": 4 * mm});
            skCircle(sketch, "E79.6", {"center": v(-60, 67.5) * mm, "radius": 4 * mm});
            skArc(sketch, "E79.7", {"start": v(80, 80) * mm, "mid": v(77.07, 87.07) * mm, "end": v(70, 90) * mm});
            skLineSegment(sketch, "E79.8", {"start": v(80, -80) * mm, "end": v(80, 80) * mm});
            skArc(sketch, "E79.9", {"start": v(70, -90) * mm, "mid": v(77.07, -87.07) * mm, "end": v(80, -80) * mm});
            skCircle(sketch, "E79.17", {"center": v(60, 67.5) * mm, "radius": 4 * mm});
            skCircle(sketch, "E79.18", {"center": v(60, -67.5) * mm, "radius": 4 * mm});
            skArc(sketch, "E80.0", {"start": v(56.15, 48.18) * mm, "mid": v(0, 67.5) * mm, "end": v(-56.15, 48.18) * mm});
            skLineSegment(sketch, "E80.1", {"start": v(-60, 40.3) * mm, "end": v(-60, -40.3) * mm});
            skArc(sketch, "E80.2", {"start": v(-56.15, 48.18) * mm, "mid": v(-58.99, 44.68) * mm, "end": v(-60, 40.3) * mm});
            skArc(sketch, "E80.3", {"start": v(-60, -40.3) * mm, "mid": v(-58.99, -44.68) * mm, "end": v(-56.15, -48.18) * mm});
            skArc(sketch, "E80.4", {"start": v(-56.15, -48.18) * mm, "mid": v(0, -67.5) * mm, "end": v(56.15, -48.18) * mm});
            skArc(sketch, "E80.5", {"start": v(56.15, -48.18) * mm, "mid": v(58.99, -44.68) * mm, "end": v(60, -40.3) * mm});
            skLineSegment(sketch, "E80.6", {"start": v(60, 40.3) * mm, "end": v(60, -40.3) * mm});
            skArc(sketch, "E80.7", {"start": v(60, 40.3) * mm, "mid": v(58.99, 44.68) * mm, "end": v(56.15, 48.18) * mm});
            skPoint(sketch, "E80.8", {"position": v(58.99, -44.68) * mm});
            skPoint(sketch, "E80.9", {"position": v(58.99, -44.68) * mm});
            skLineSegment(sketch, "E81", {"start": v(0, 90) * mm, "end": v(0, 120) * mm, "construction": true});
            skCircle(sketch, "E82", {"center": v(0, 120) * mm, "radius": 6 * mm});
            skArc(sketch, "E83", {"start": v(15, 120) * mm, "mid": v(0, 135) * mm, "end": v(-15, 120) * mm});
            skLineSegment(sketch, "E84", {"start": v(-15, 120) * mm, "end": v(-15, 108) * mm});
            skLineSegment(sketch, "E85", {"start": v(-15, 108) * mm, "end": v(-33, 90) * mm});
            skLineSegment(sketch, "E86.1", {"start": v(-70, 90) * mm, "end": v(70, 90) * mm});
            skLineSegment(sketch, "E87.MirrorCS", {"start": v(15, 120) * mm, "end": v(15, 108) * mm});
            skLineSegment(sketch, "E88.MirrorCS", {"start": v(15, 108) * mm, "end": v(33, 90) * mm});
            skLineSegment(sketch, "E89", {"start": v(-80, 0) * mm, "end": v(80, 0) * mm, "construction": true});
            skArc(sketch, "E90.MirrorCS", {"start": v(-15, 120) * mm, "mid": v(0, 135) * mm, "end": v(15, 120) * mm});
            skLineSegment(sketch, "E91.MirrorCS", {"start": v(70, 90) * mm, "end": v(-70, 90) * mm});
            skLineSegment(sketch, "E92.MirrorCS", {"start": v(15, -108) * mm, "end": v(33, -90) * mm});
            skLineSegment(sketch, "E93.MirrorCS", {"start": v(-15, -108) * mm, "end": v(-33, -90) * mm});
            skLineSegment(sketch, "E94.MirrorCS", {"start": v(-15, -120) * mm, "end": v(-15, -108) * mm});
            skArc(sketch, "E95.MirrorCS", {"start": v(-15, -120) * mm, "mid": v(0, -135) * mm, "end": v(15, -120) * mm});
            skLineSegment(sketch, "E96.MirrorCS", {"start": v(15, -120) * mm, "end": v(15, -108) * mm});
            skArc(sketch, "E97.MirrorCS", {"start": v(15, -120) * mm, "mid": v(0, -135) * mm, "end": v(-15, -120) * mm});
            skCircle(sketch, "E98.MirrorC", {"center": v(0, -120) * mm, "radius": 6 * mm});
            skLineSegment(sketch, "E99.MirrorCS", {"start": v(0, -90) * mm, "end": v(0, -120) * mm, "construction": true});
            skSolve(sketch);
        }
        {
            var Q0;
            Q0=makeQuery(id+"F16.imprint","IMPRINT",FACE,{"disambiguationData":[TD([[makeQuery(id+"F16.imprint","IMPRINT",EDGE,{"derivedFrom":sQuery(id+"F16.wireOp",EDGE,"E84")}),1.0]])]});
            var Q1;
            {var subQ1=sQuery(id+"F16.wireOp",EDGE,"E93.MirrorCS");Q1=makeQuery(id+"F16.imprint","IMPRINT",FACE,{"disambiguationData":[TD([[makeQuery(id+"F16.imprint","IMPRINT",EDGE,{"derivedFrom":subQ1}),-1.0]])]});}
            var Q2;
            {var subQ4=sQuery(id+"F16.wireOp",EDGE,"E79.1");Q2=makeQuery(id+"F16.imprint","IMPRINT",FACE,{"disambiguationData":[TD([[makeQuery(id+"F16.imprint","IMPRINT",EDGE,{"derivedFrom":subQ4}),1.0]])]});}
            var Q3;
            Q3=makeQuery(id+"F2.opExtrude","CAP_FACE",FACE,{"disambiguationData":[OSD([sQuery(id+"F0.wireOp",EDGE,"E12"),sQuery(id+"F0.wireOp",EDGE,"E13"),sQuery(id+"F0.wireOp",EDGE,"E14"),sQuery(id+"F0.wireOp",EDGE,"E15"),sQuery(id+"F0.wireOp",EDGE,"E17.filletArc"),sQuery(id+"F0.wireOp",EDGE,"E18.filletArc"),sQuery(id+"F0.wireOp",EDGE,"E19.filletArc"),sQuery(id+"F0.wireOp",EDGE,"E20.filletArc"),sQuery(id+"F0.wireOp",EDGE,"E25.0"),sQuery(id+"F0.wireOp",EDGE,"E25.1"),sQuery(id+"F0.wireOp",EDGE,"E25.2"),sQuery(id+"F0.wireOp",EDGE,"E25.3"),sQuery(id+"F0.wireOp",EDGE,"E25.4"),sQuery(id+"F0.wireOp",EDGE,"E25.5"),sQuery(id+"F0.wireOp",EDGE,"E25.6"),sQuery(id+"F0.wireOp",EDGE,"E25.7")])],"isStart":false});
            extrude(context, id + "F17", {"entities" : qUnion([Q0, Q1, Q2]), "endBound" : BoundingType.UP_TO_SURFACE, "endBoundEntityFace" : qUnion([Q3]), "depth" : 25 * mm});
        }
    });
